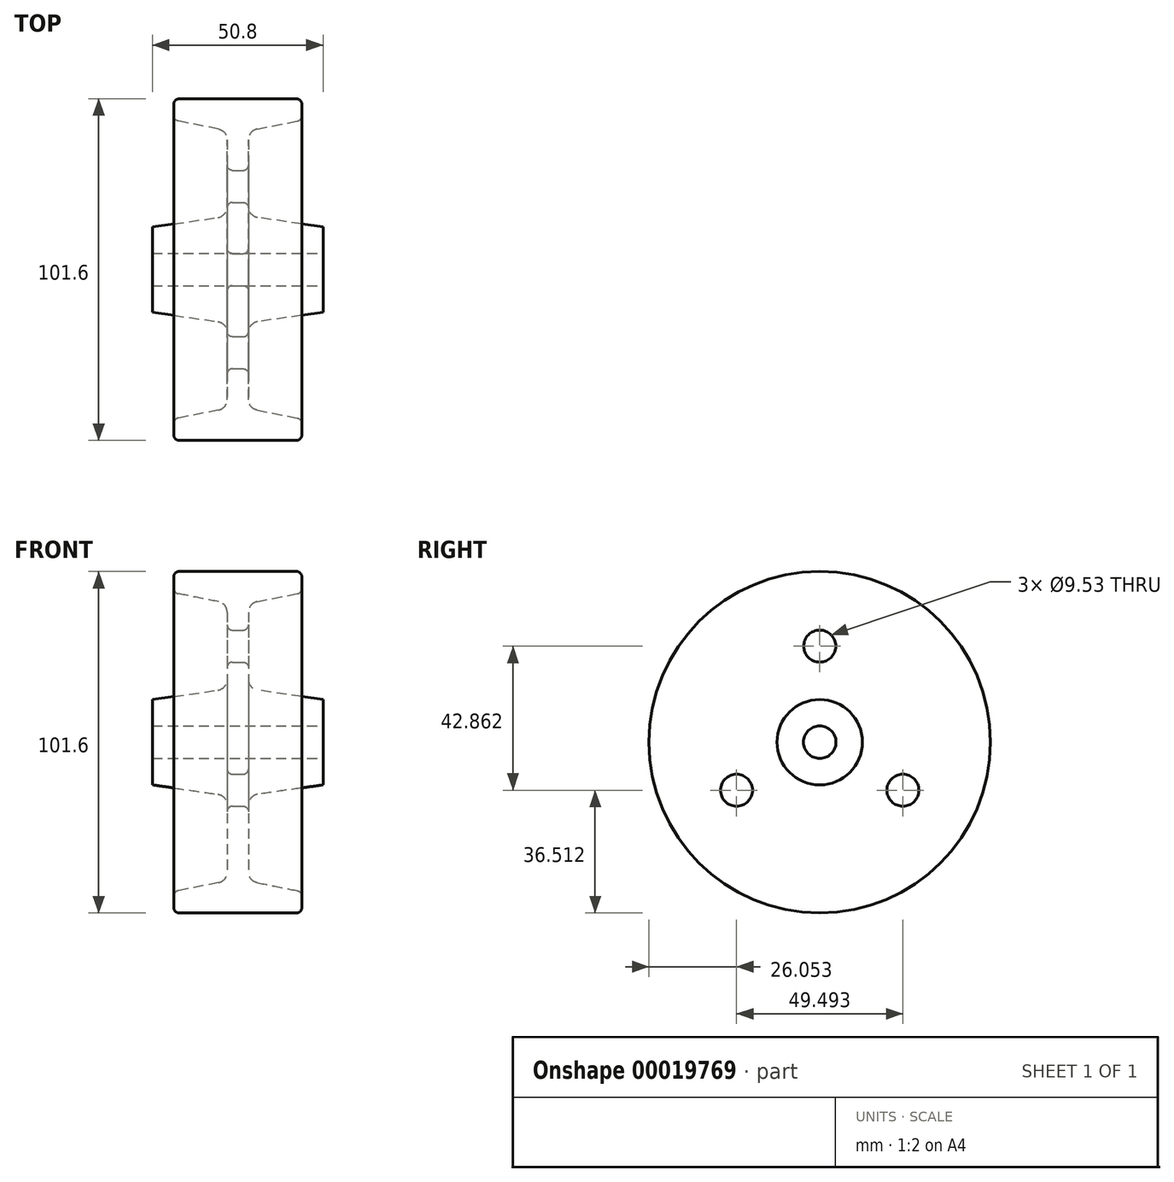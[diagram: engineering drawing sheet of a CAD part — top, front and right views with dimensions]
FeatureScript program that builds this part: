
annotation { "Feature Type Name" : "Feature", "Feature Type Description" : "" }
export const myFeature = defineFeature(function(context is Context, id is Id, definition is map)
    precondition{}
    {
        {
            var Q0;
            Q0=qCreatedBy(makeId("Front.planeOp"),FACE);
            var sketch = newSketch(context, id + "F0", { "sketchPlane" : qUnion([Q0])});
            skLineSegment(sketch, "E0", {"start": v(-19.05, 50.8) * mm, "end": v(0, 50.8) * mm});
            skLineSegment(sketch, "E1", {"start": v(-19.05, 50.8) * mm, "end": v(-19.05, 44.45) * mm});
            skLineSegment(sketch, "E2", {"start": v(-3.17, 41.28) * mm, "end": v(-3.17, 15.88) * mm});
            skLineSegment(sketch, "E3", {"start": v(-19.05, 44.45) * mm, "end": v(-3.17, 41.28) * mm});
            skPoint(sketch, "E4.start.orphan", {"position": v(-3.18, 50.8) * mm});
            skLineSegment(sketch, "E5", {"start": v(0, 0) * mm, "end": v(-25.4, 0) * mm});
            skLineSegment(sketch, "E6", {"start": v(-25.4, 0) * mm, "end": v(-25.4, 12.7) * mm});
            skLineSegment(sketch, "E7", {"start": v(-25.4, 12.7) * mm, "end": v(-3.17, 15.88) * mm});
            skPoint(sketch, "E8.start.orphan", {"position": v(-3.17, 0) * mm});
            skLineSegment(sketch, "E9.MirrorCS", {"start": v(25.4, 12.7) * mm, "end": v(3.17, 15.88) * mm});
            skLineSegment(sketch, "E10.MirrorCS", {"start": v(25.4, 0) * mm, "end": v(25.4, 12.7) * mm});
            skPoint(sketch, "E11.MirrorP", {"position": v(3.18, 50.8) * mm});
            skLineSegment(sketch, "E12.MirrorCS", {"start": v(19.05, 44.45) * mm, "end": v(3.17, 41.28) * mm});
            skLineSegment(sketch, "E13.MirrorCS", {"start": v(19.05, 50.8) * mm, "end": v(19.05, 44.45) * mm});
            skLineSegment(sketch, "E14.MirrorCS", {"start": v(3.17, 41.28) * mm, "end": v(3.17, 15.88) * mm});
            skPoint(sketch, "E15.MirrorP", {"position": v(3.17, 0) * mm});
            skLineSegment(sketch, "E16", {"start": v(0, 50.8) * mm, "end": v(19.05, 50.8) * mm});
            skLineSegment(sketch, "E17", {"start": v(0, 0) * mm, "end": v(25.4, 0) * mm});
            skSolve(sketch);
        }
        {
            var Q0;
            Q0=makeQuery(id+"F0.imprint","IMPRINT",FACE,{"disambiguationData":[TD([[makeQuery(id+"F0.imprint","IMPRINT",EDGE,{"derivedFrom":sQuery(id+"F0.wireOp",EDGE,"E0")}),-1.0]])]});
            var Q1;
            Q1=sQuery(id+"F0.wireOp",EDGE,"E5");
            revolve(context, id + "F1", {"entities" : qUnion([Q0]), "axis" : qUnion([Q1]), "revolveType" : RevolveType.FULL});
        }
        {
            var Q0;
            Q0=qCreatedBy(makeId("Right.planeOp"),FACE);
            var sketch = newSketch(context, id + "F2", { "sketchPlane" : qUnion([Q0])});
            skCircle(sketch, "E18", {"center": v(0, 0) * mm, "radius": 4.83 * mm});
            skCircle(sketch, "E19", {"center": v(0, 0) * mm, "radius": 28.58 * mm, "construction": true});
            skCircle(sketch, "E20", {"center": v(0, 28.58) * mm, "radius": 4.76 * mm});
            skCircle(sketch, "E21.1.0", {"center": v(-24.75, -14.29) * mm, "radius": 4.76 * mm});
            skCircle(sketch, "E21.2.0", {"center": v(24.75, -14.29) * mm, "radius": 4.76 * mm});
            skSolve(sketch);
        }
        {
            var Q0;
            Q0 = qSketchRegion(id + "F2", true);
            extrude(context, id + "F3", {"entities" : qUnion([Q0]), "operationType" : NewBodyOperationType.REMOVE, "endBound" : BoundingType.SYMMETRIC, "oppositeDirection" : true, "depth" : 254 * mm});
        }
        {
            var Q0;
            Q0=makeQuery(id+"F1.opRevolve","SWEPT_EDGE",EDGE,{"disambiguationData":[OSD([sQuery(id+"F0.wireOp",EDGE,"E12.MirrorCS"),sQuery(id+"F0.wireOp",EDGE,"E13.MirrorCS")])]});
            var Q1;
            Q1=makeQuery(id+"F1.opRevolve","SWEPT_EDGE",EDGE,{"disambiguationData":[OSD([sQuery(id+"F0.wireOp",EDGE,"E13.MirrorCS"),sQuery(id+"F0.wireOp",EDGE,"E16")])]});
            var Q2;
            Q2=makeQuery(id+"F3.boolean.opBoolean","INTERSECT",EDGE,{"derivedFrom":[makeQuery(id+"F1.opRevolve","SWEPT_FACE",FACE,{"disambiguationData":[OSD([sQuery(id+"F0.wireOp",EDGE,"E14.MirrorCS")])]}),makeQuery(id+"F3.opExtrude","SWEPT_FACE",FACE,{"disambiguationData":[OSD([sQuery(id+"F2.wireOp",EDGE,"E20")])]})]});
            var Q3;
            Q3=makeQuery(id+"F3.boolean.opBoolean","INTERSECT",EDGE,{"derivedFrom":[makeQuery(id+"F1.opRevolve","SWEPT_FACE",FACE,{"disambiguationData":[OSD([sQuery(id+"F0.wireOp",EDGE,"E14.MirrorCS")])]}),makeQuery(id+"F3.opExtrude","SWEPT_FACE",FACE,{"disambiguationData":[OSD([sQuery(id+"F2.wireOp",EDGE,"E21.1.0")])]})]});
            var Q4;
            Q4=makeQuery(id+"F3.boolean.opBoolean","INTERSECT",EDGE,{"derivedFrom":[makeQuery(id+"F1.opRevolve","SWEPT_FACE",FACE,{"disambiguationData":[OSD([sQuery(id+"F0.wireOp",EDGE,"E14.MirrorCS")])]}),makeQuery(id+"F3.opExtrude","SWEPT_FACE",FACE,{"disambiguationData":[OSD([sQuery(id+"F2.wireOp",EDGE,"E21.2.0")])]})]});
            var Q5;
            Q5=makeQuery(id+"F1.opRevolve","SWEPT_EDGE",EDGE,{"disambiguationData":[OSD([sQuery(id+"F0.wireOp",EDGE,"E0"),sQuery(id+"F0.wireOp",EDGE,"E1")])]});
            var Q6;
            Q6=makeQuery(id+"F1.opRevolve","SWEPT_EDGE",EDGE,{"disambiguationData":[OSD([sQuery(id+"F0.wireOp",EDGE,"E1"),sQuery(id+"F0.wireOp",EDGE,"E3")])]});
            var Q7;
            Q7=makeQuery(id+"F3.boolean.opBoolean","INTERSECT",EDGE,{"derivedFrom":[makeQuery(id+"F1.opRevolve","SWEPT_FACE",FACE,{"disambiguationData":[OSD([sQuery(id+"F0.wireOp",EDGE,"E2")])]}),makeQuery(id+"F3.opExtrude","SWEPT_FACE",FACE,{"disambiguationData":[OSD([sQuery(id+"F2.wireOp",EDGE,"E20")])]})]});
            var Q8;
            Q8=makeQuery(id+"F3.boolean.opBoolean","INTERSECT",EDGE,{"derivedFrom":[makeQuery(id+"F1.opRevolve","SWEPT_FACE",FACE,{"disambiguationData":[OSD([sQuery(id+"F0.wireOp",EDGE,"E2")])]}),makeQuery(id+"F3.opExtrude","SWEPT_FACE",FACE,{"disambiguationData":[OSD([sQuery(id+"F2.wireOp",EDGE,"E21.1.0")])]})]});
            var Q9;
            Q9=makeQuery(id+"F3.boolean.opBoolean","INTERSECT",EDGE,{"derivedFrom":[makeQuery(id+"F1.opRevolve","SWEPT_FACE",FACE,{"disambiguationData":[OSD([sQuery(id+"F0.wireOp",EDGE,"E2")])]}),makeQuery(id+"F3.opExtrude","SWEPT_FACE",FACE,{"disambiguationData":[OSD([sQuery(id+"F2.wireOp",EDGE,"E21.2.0")])]})]});
            fillet(context, id + "F4", {"entities" : qUnion([Q0, Q1, Q2, Q3, Q4, Q5, Q6, Q7, Q8, Q9]), "radius" : 1.59 * mm, "tangentPropagation" : true, "allowEdgeOverflow" : false});
        }
        {
            var Q0;
            Q0=makeQuery(id+"F1.opRevolve","SWEPT_EDGE",EDGE,{"disambiguationData":[OSD([sQuery(id+"F0.wireOp",EDGE,"E2"),sQuery(id+"F0.wireOp",EDGE,"E7")])]});
            var Q1;
            Q1=makeQuery(id+"F1.opRevolve","SWEPT_EDGE",EDGE,{"disambiguationData":[OSD([sQuery(id+"F0.wireOp",EDGE,"E2"),sQuery(id+"F0.wireOp",EDGE,"E3")])]});
            var Q2;
            Q2=makeQuery(id+"F1.opRevolve","SWEPT_EDGE",EDGE,{"disambiguationData":[OSD([sQuery(id+"F0.wireOp",EDGE,"E12.MirrorCS"),sQuery(id+"F0.wireOp",EDGE,"E14.MirrorCS")])]});
            var Q3;
            Q3=makeQuery(id+"F1.opRevolve","SWEPT_EDGE",EDGE,{"disambiguationData":[OSD([sQuery(id+"F0.wireOp",EDGE,"E9.MirrorCS"),sQuery(id+"F0.wireOp",EDGE,"E14.MirrorCS")])]});
            fillet(context, id + "F5", {"entities" : qUnion([Q0, Q1, Q2, Q3]), "radius" : 3.17 * mm, "tangentPropagation" : true, "allowEdgeOverflow" : false});
        }
    });
